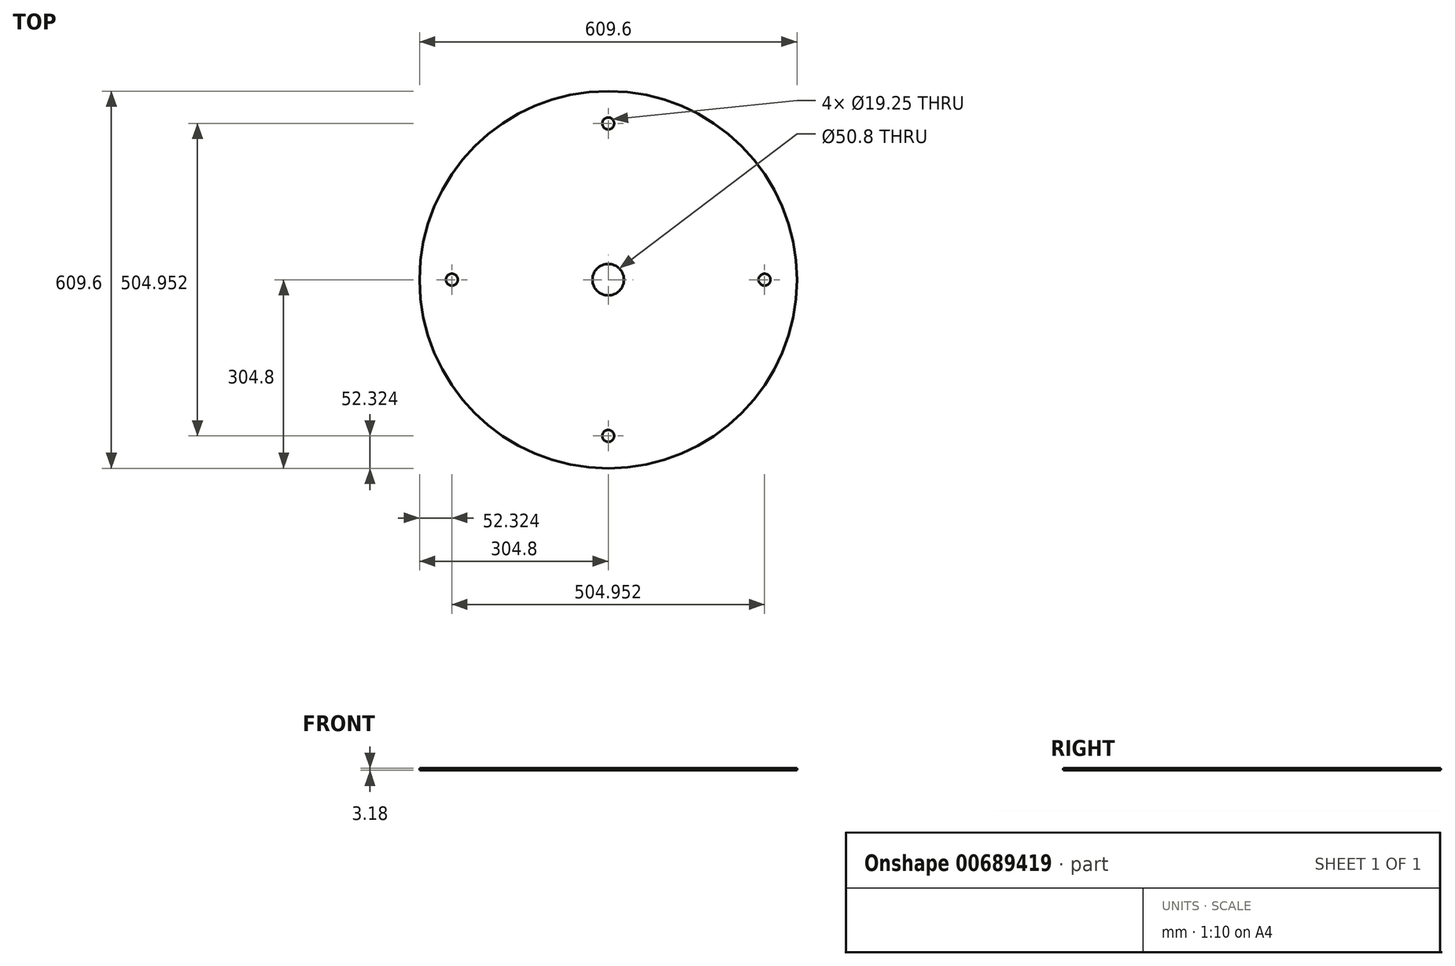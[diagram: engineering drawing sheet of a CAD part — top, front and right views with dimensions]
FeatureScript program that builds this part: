
annotation { "Feature Type Name" : "Feature", "Feature Type Description" : "" }
export const myFeature = defineFeature(function(context is Context, id is Id, definition is map)
    precondition{}
    {
        {
            var Q0;
            Q0=qCreatedBy(makeId("Top.planeOp"),FACE);
            var sketch = newSketch(context, id + "F0", { "sketchPlane" : qUnion([Q0])});
            skCircle(sketch, "E0", {"center": v(0, 0) * mm, "radius": 304.8 * mm});
            skCircle(sketch, "E1", {"center": v(252.48, 0) * mm, "radius": 9.63 * mm});
            skCircle(sketch, "E2.1.0", {"center": v(0, 252.48) * mm, "radius": 9.63 * mm});
            skCircle(sketch, "E2.2.0", {"center": v(-252.48, 0) * mm, "radius": 9.63 * mm});
            skCircle(sketch, "E2.3.0", {"center": v(0, -252.48) * mm, "radius": 9.63 * mm});
            skCircle(sketch, "E3", {"center": v(0, 0) * mm, "radius": 25.4 * mm});
            skSolve(sketch);
        }
        {
            var Q0;
            Q0=makeQuery(id+"F0.imprint","IMPRINT",FACE,{"disambiguationData":[TD([[makeQuery(id+"F0.imprint","IMPRINT",EDGE,{"derivedFrom":sQuery(id+"F0.wireOp",EDGE,"E0")}),1.0]])]});
            extrude(context, id + "F1", {"entities" : qUnion([Q0]), "depth" : 3.17 * mm, "offsetDistance" : 25.4 * mm});
        }
    });
